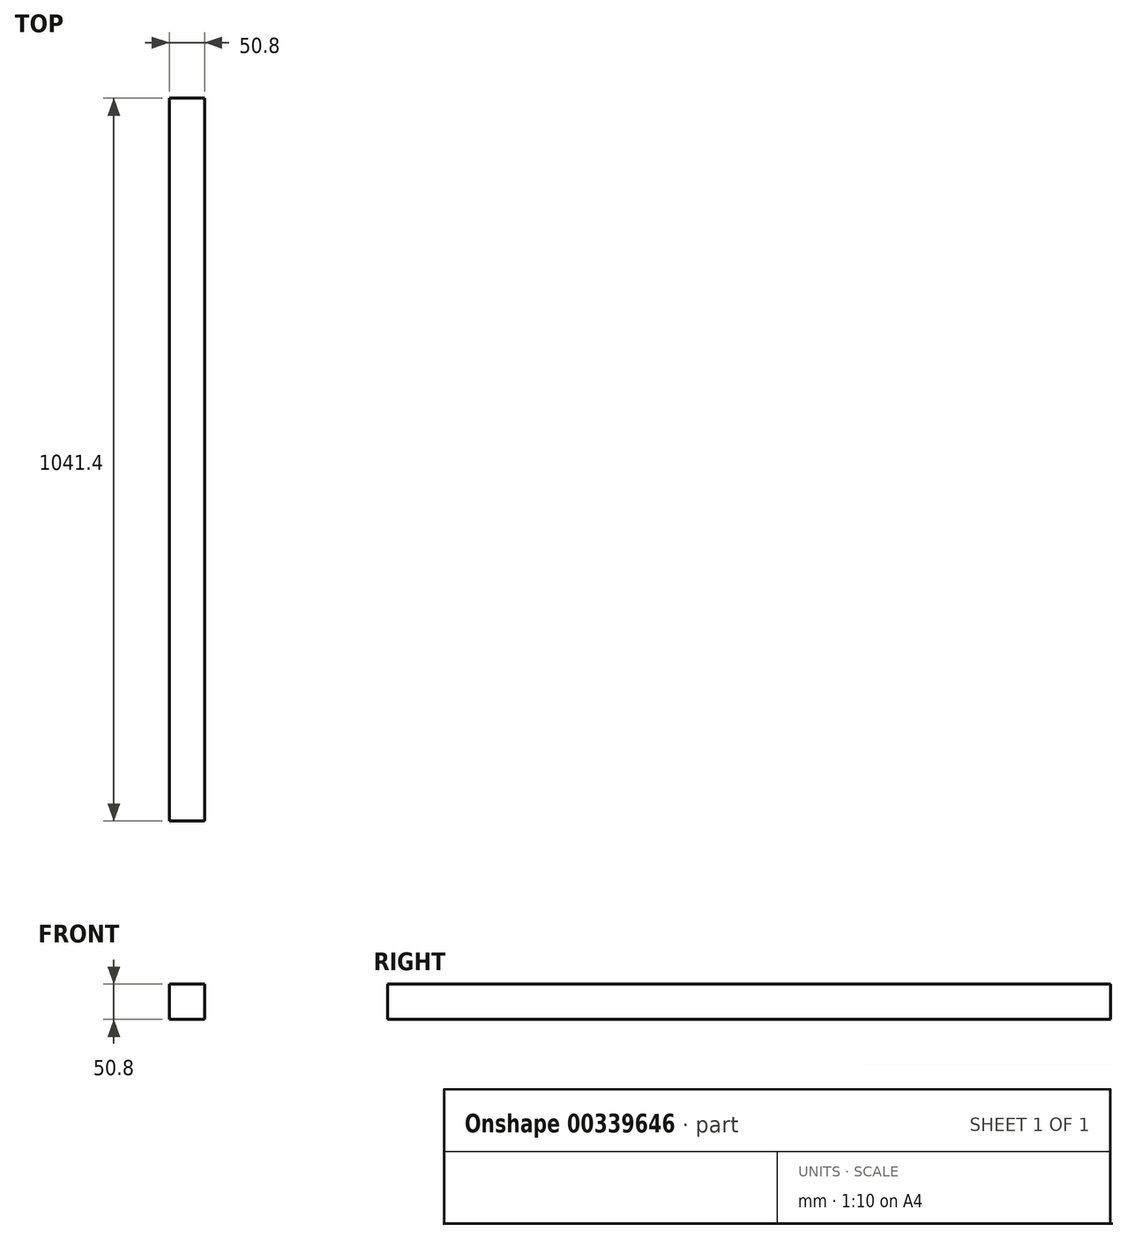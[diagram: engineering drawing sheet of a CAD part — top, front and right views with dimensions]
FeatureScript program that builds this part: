
annotation { "Feature Type Name" : "Feature", "Feature Type Description" : "" }
export const myFeature = defineFeature(function(context is Context, id is Id, definition is map)
    precondition{}
    {
        {
            var Q0;
            Q0=qCreatedBy(makeId("Front.planeOp"),FACE);
            var sketch = newSketch(context, id + "F0", { "sketchPlane" : qUnion([Q0])});
            skLineSegment(sketch, "E0.bottom", {"start": v(0, 0) * mm, "end": v(50.8, 0) * mm});
            skLineSegment(sketch, "E0.top", {"start": v(0, 50.8) * mm, "end": v(50.8, 50.8) * mm});
            skLineSegment(sketch, "E0.left", {"start": v(0, 0) * mm, "end": v(0, 50.8) * mm});
            skLineSegment(sketch, "E0.right", {"start": v(50.8, 0) * mm, "end": v(50.8, 50.8) * mm});
            skSolve(sketch);
        }
        {
            var Q0;
            Q0=makeQuery(id+"F0.imprint","IMPRINT",FACE,{"disambiguationData":[TD([[makeQuery(id+"F0.imprint","IMPRINT",EDGE,{"derivedFrom":sQuery(id+"F0.wireOp",EDGE,"E0.bottom")}),1.0]])]});
            extrude(context, id + "F1", {"entities" : qUnion([Q0]), "depth" : 1041.4 * mm});
        }
    });
